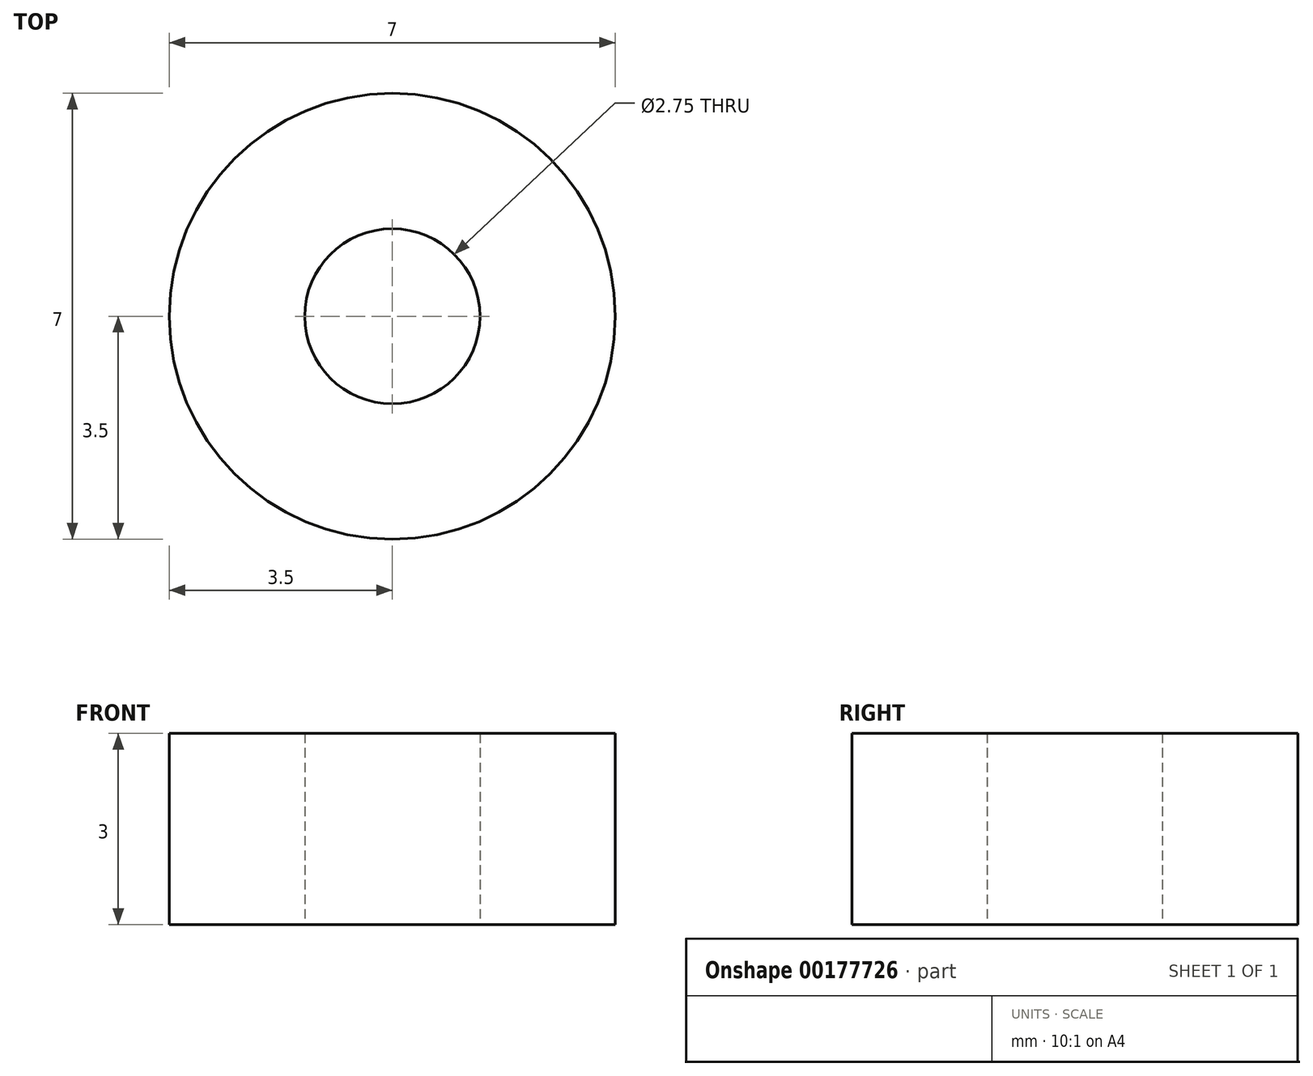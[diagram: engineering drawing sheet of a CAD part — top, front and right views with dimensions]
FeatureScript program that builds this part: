
annotation { "Feature Type Name" : "Feature", "Feature Type Description" : "" }
export const myFeature = defineFeature(function(context is Context, id is Id, definition is map)
    precondition{}
    {
        {
            var Q0;
            Q0=qCreatedBy(makeId("Top.planeOp"),FACE);
            var sketch = newSketch(context, id + "F0", { "sketchPlane" : qUnion([Q0])});
            skCircle(sketch, "E0", {"center": v(0, 0) * mm, "radius": 3.5 * mm});
            skSolve(sketch);
        }
        {
            var Q0;
            Q0=makeQuery(id+"F0.imprint","IMPRINT",FACE,{"disambiguationData":[TD([[makeQuery(id+"F0.imprint","IMPRINT",EDGE,{"derivedFrom":sQuery(id+"F0.wireOp",EDGE,"E0")}),1.0]])]});
            extrude(context, id + "F1", {"entities" : qUnion([Q0]), "depth" : 3 * mm});
        }
        {
            var Q0;
            Q0=makeQuery(id+"F1.opExtrude","CAP_FACE",FACE,{"disambiguationData":[OSD([sQuery(id+"F0.wireOp",EDGE,"E0")])],"isStart":true});
            var sketch = newSketch(context, id + "F2", { "sketchPlane" : qUnion([Q0])});
            skCircle(sketch, "E1", {"center": v(0, 0) * mm, "radius": 1.38 * mm});
            skSolve(sketch);
        }
        {
            var Q0;
            Q0=sQuery(id+"F2.wireOp",VERTEX,"E1.center");
            var Q1;
            Q1=makeQuery(id+"F1.opExtrude","SWEPT_BODY",BODY,{"disambiguationData":[OSD([sQuery(id+"F0.wireOp",EDGE,"E0")])]});
            hole(context, id + "F3", {"style" : HoleStyle.SIMPLE, "endStyle" : HoleEndStyle.BLIND, "holeDiameter" : 2.75 * mm, "holeDepth" : 30 * mm, "startFromSketch" : true, "locations" : qUnion([Q0]), "scope" : qUnion([Q1])});
        }
    });
